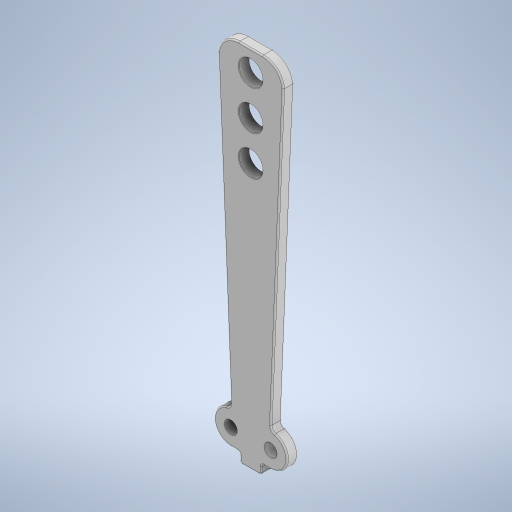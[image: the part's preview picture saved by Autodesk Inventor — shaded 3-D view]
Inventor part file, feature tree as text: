
AUTODESK INVENTOR PART (.ipt)
format: ipt  version: 2023.5 (Build 275446000, 446)  size: 385,024 bytes
history: native  units: mm
features: extrude x2, fillet x2, sketch x2, chamfer x1, projected_geometry x1
ambient origin geometry x8: Origin, YZ Plane, XZ Plane, XY Plane, X Axis, Y Axis, Z Axis, Center Point
bodies: Solid1 (feature_tree)
feature tree (8):
  extrude  "Extrusion1"  Depth=24.987954mm
  fillet  "Fillet1"  Radius=0.841608mm
  extrude  "Extrusion2"  Depth=4.077mm
  fillet  "Fillet3"  Radius=4.077mm
  chamfer  "Chamfer1"  Distance=8.0mm
  sketch  "Sketch1"  dims[d2=15.239999mm d15=4.572mm d16=24.987954mm d17=0.841608mm]
  sketch  "Sketch2"  dims[d74=10.160001mm d75=3.948149mm d102=4.077mm d103=0.0mm d104=8.0mm d114=15.0mm d115=15.0mm d118=23.0mm d119=38.0mm d120=0.0mm d121=0.0mm d122=2.0mm d124=0.5mm d125=0.2mm d126=2.0mm d127=45.0deg d105=0.0mm d106=0.0mm d107=0.0mm d123=0.0mm]
  projected_geometry  "Projected Loop1"
